# Revit family: HPR17HT
name_source: partatom
category: Mechanical Equipment
units: mm (PartAtom-declared; Revit-internal decimal feet)

## family parameters
Always vertical = Yes
Cut with Voids When Loaded = No
OmniClass Number = 23.75.00.00
OmniClass Title = Climate Control (HVAC)
Part Type = Normal
Room Calculation Point = No
Round Connector Dimension = Use Diameter
Shared = No
Work Plane-Based = No

## types (1)
- HPR17HT
    Base = 800 mm  [stored 2.62467 ft]
    Connection Size = 25 mm
    Default Elevation = 0 mm  [stored 0 ft]
    Length = 1247 mm  [stored 4.09121 ft]
    Max Heating Capacity = 22.00 kW
    Max Output Temperature = 75 °C
    Max Power Input = 7 W
    Maximum Current Input = 32 A
    Min Heating Capacity = 8.00 kW
    Overal Width = 540 mm  [stored 1.77165 ft]
    Overall Height = 1329 mm  [stored 4.36024 ft]
    Pump Pressure = 73.6 Pa
    Refrigerant = R290
    Width = 515 mm  [stored 1.68963 ft]

note: [stored X ft] marks values corroborated as IEEE doubles in the binary element streams (Revit-internal decimal feet)

## geometry (parser evidence)
native form markers: Sweep x3
no freeform markers — native parametric forms only
